# Revit family: Sanitary_Showers_AXOR_36715CHN-AXOR-ShowerSolutions-Thermostat_55
name_source: partatom
category: Plumbing Fixtures
revit_build: Autodesk Revit 2018 (Build: 20170223_1515(x64)
units: mm (PartAtom-declared; Revit-internal decimal feet)

## family parameters
Always vertical = No
Cut with Voids When Loaded = No
OmniClass Number = 23.31.17.19
OmniClass Title = Shower Head Fixtures
Part Type = Normal
Room Calculation Point = No
Round Connector Dimension = Use Diameter
Shared = No
Work Plane-Based = Yes

## types (5) — shared parameters
Always visible = Yes
BIMobject category = Showers
Default Elevation = 1219.2 mm  [stored 4 ft]
Description = AXOR ShowerSolutions Thermostat for concealed installation square for 2 functions
Design country = Germany
EAN code = 4059625130834
Edition number = 1
GTIN code = https://4059625130834
IFC Classification = Sanitary Terminal
Installation instructions = https://www.axor-design.com
Manufacturer = AXOR
Manufacturer country = Germany
Manufacturer name = AXOR
Material 1 = AXOR - Plastic - Dark Gray
Model = 36715CHN
OmniClass Code = 23-31 17 19
OmniClass Description = Shower Head Fixtures
Product Guid = 362a20e0-c2d5-4d1a-a724-515778b8f85c
Product SKU = 36715CHN
Product data url = https://bimobject.com
Product family = AXOR ShowerSolutions
Product group = Shower thermostat
Product name = 36715CHN AXOR ShowerSolutions Thermostat for concealed installation square for 2 functions
Product url = https://www.axor-design.com
QR code = https://bimobject.com
URL = https://www.axor-design.com
Weight Net (Kg) = 2

## per-type parameters (varying)
| type | Material 2 |
| 677 Matt Black | AXOR - Metal - 677 Matt Black |
| 007 Chrome | AXOR - Metal - 007 Chrome |
| 347 Brushed Black Chrome | AXOR - Metal - 347 Brushed Black Chrome |
| 357 Satin Black | AXOR - Metal - 357 Satin Black |
| 997 Polished Gold Optic | AXOR - Metal - 997 Polished Gold Optic |

note: [stored X ft] marks values corroborated as IEEE doubles in the binary element streams (Revit-internal decimal feet)

## geometry (parser evidence)
native form markers: Sweep x2
no freeform markers — native parametric forms only
